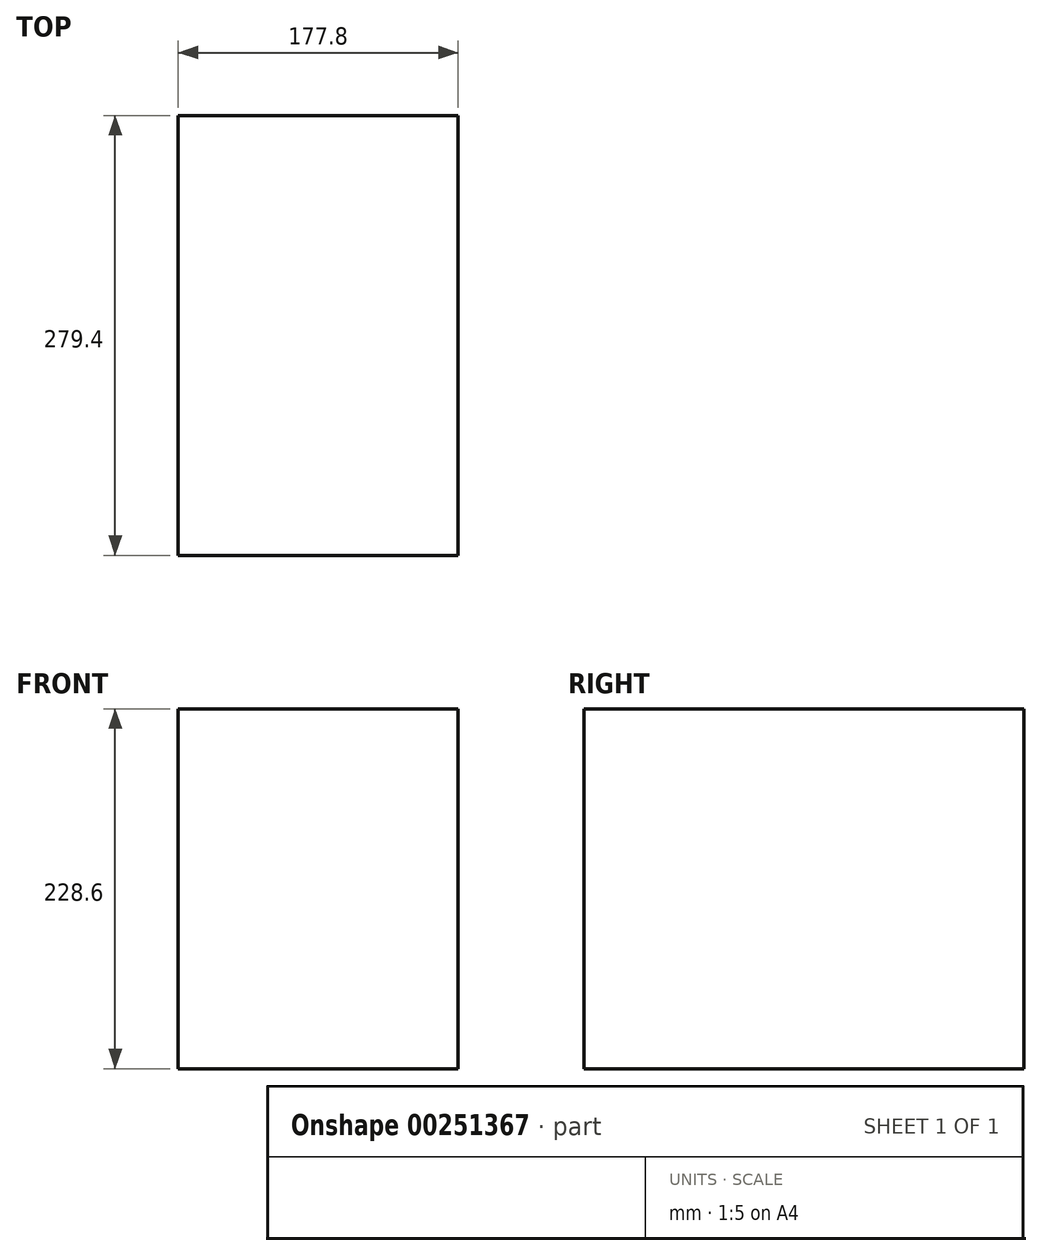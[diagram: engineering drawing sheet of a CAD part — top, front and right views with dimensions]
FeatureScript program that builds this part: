
annotation { "Feature Type Name" : "Feature", "Feature Type Description" : "" }
export const myFeature = defineFeature(function(context is Context, id is Id, definition is map)
    precondition{}
    {
        {
            var Q0;
            Q0=qCreatedBy(makeId("Front.planeOp"),FACE);
            var sketch = newSketch(context, id + "F0", { "sketchPlane" : qUnion([Q0])});
            skLineSegment(sketch, "E0.bottom", {"start": v(88.9, -114.3) * mm, "end": v(-88.9, -114.3) * mm});
            skLineSegment(sketch, "E0.top", {"start": v(88.9, 114.3) * mm, "end": v(-88.9, 114.3) * mm});
            skLineSegment(sketch, "E0.left", {"start": v(88.9, -114.3) * mm, "end": v(88.9, 114.3) * mm});
            skLineSegment(sketch, "E0.right", {"start": v(-88.9, -114.3) * mm, "end": v(-88.9, 114.3) * mm});
            skPoint(sketch, "E0.middle", {"position": v(0, 0) * mm});
            skSolve(sketch);
        }
        {
            var Q0;
            Q0 = qSketchRegion(id + "F0", true);
            extrude(context, id + "F1", {"entities" : qUnion([Q0]), "endBound" : BoundingType.SYMMETRIC, "depth" : 279.4 * mm});
        }
    });
